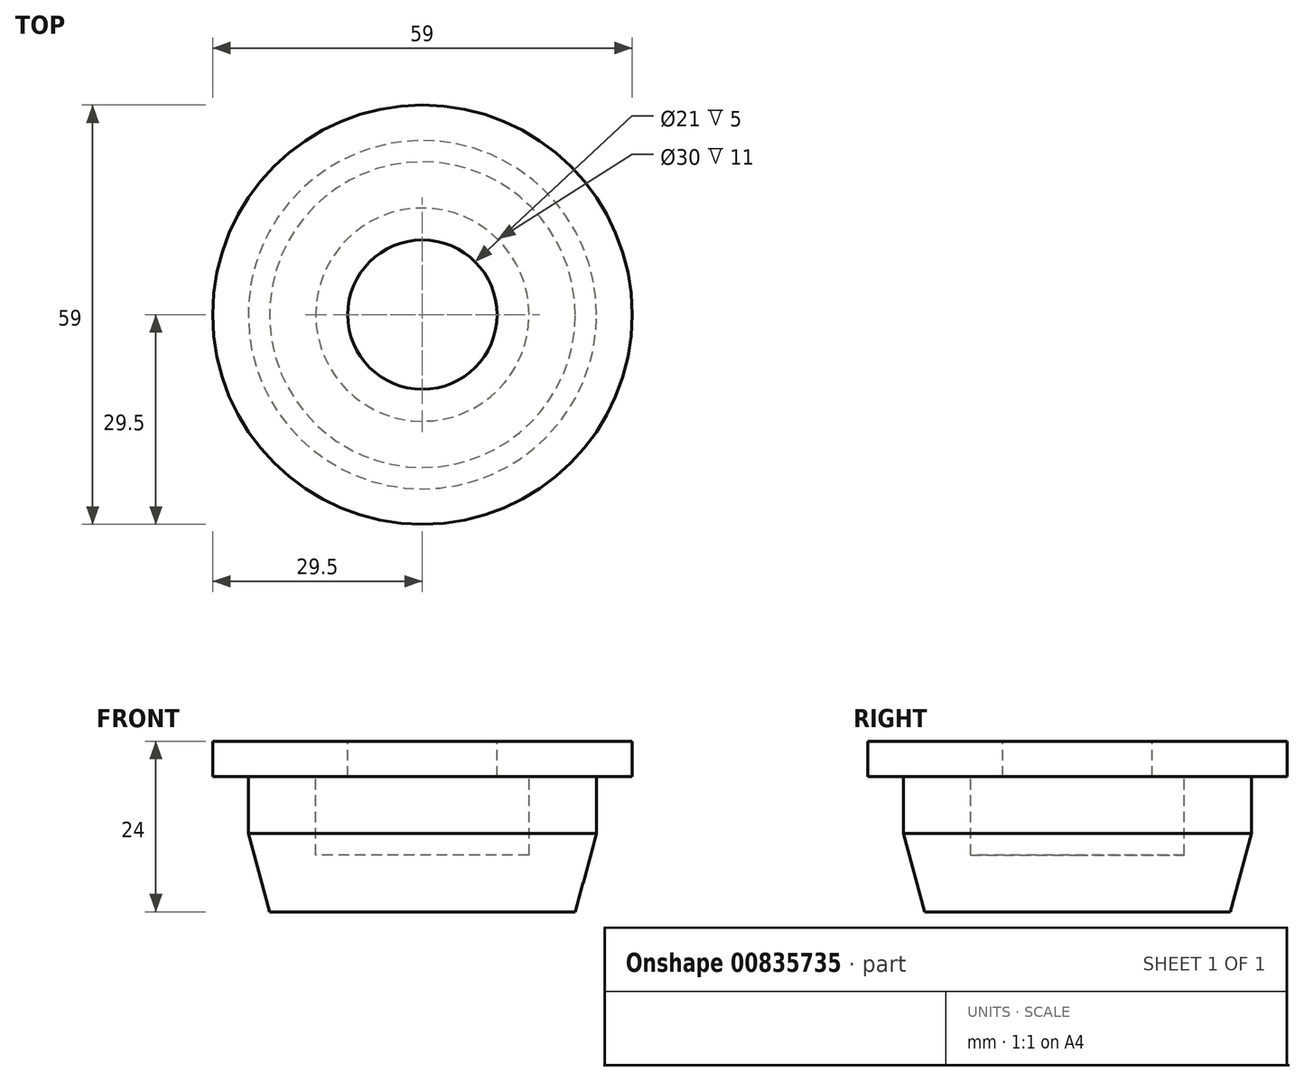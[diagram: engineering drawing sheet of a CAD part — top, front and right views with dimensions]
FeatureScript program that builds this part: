
annotation { "Feature Type Name" : "Feature", "Feature Type Description" : "" }
export const myFeature = defineFeature(function(context is Context, id is Id, definition is map)
    precondition{}
    {
        {
            var Q0;
            Q0=qCreatedBy(makeId("Top.planeOp"),FACE);
            var sketch = newSketch(context, id + "F0", { "sketchPlane" : qUnion([Q0])});
            skCircle(sketch, "E0", {"center": v(0, 0) * mm, "radius": 10.5 * mm});
            skCircle(sketch, "E1", {"center": v(0, 0) * mm, "radius": 24.5 * mm});
            skCircle(sketch, "E2", {"center": v(0, 0) * mm, "radius": 29.5 * mm});
            skCircle(sketch, "E3", {"center": v(0, 0) * mm, "radius": 15 * mm});
            skSolve(sketch);
        }
        {
            var Q0;
            Q0=makeQuery(id+"F0.imprint","IMPRINT",FACE,{"disambiguationData":[TD([[makeQuery(id+"F0.imprint","IMPRINT",EDGE,{"derivedFrom":sQuery(id+"F0.wireOp",EDGE,"E1")}),1.0]])]});
            var Q1;
            Q1=makeQuery(id+"F0.imprint","IMPRINT",FACE,{"disambiguationData":[TD([[makeQuery(id+"F0.imprint","IMPRINT",EDGE,{"derivedFrom":sQuery(id+"F0.wireOp",EDGE,"E0")}),-1.0]])]});
            var Q2;
            Q2=makeQuery(id+"F0.imprint","IMPRINT",FACE,{"disambiguationData":[TD([[makeQuery(id+"F0.imprint","IMPRINT",EDGE,{"derivedFrom":sQuery(id+"F0.wireOp",EDGE,"E0")}),1.0]])]});
            extrude(context, id + "F1", {"entities" : qUnion([Q0, Q1, Q2]), "oppositeDirection" : true, "depth" : 24 * mm, "offsetDistance" : 25 * mm});
        }
        {
            var Q0;
            Q0=makeQuery(id+"F1.opExtrude","CAP_EDGE",EDGE,{"disambiguationData":[OSD([sQuery(id+"F0.wireOp",EDGE,"E1")])],"isStart":false});
            chamfer(context, id + "F2", {"entities" : qUnion([Q0]), "chamferType" : ChamferType.TWO_OFFSETS, "width1" : 11 * mm, "oppositeDirection" : false, "width2" : 3 * mm, "tangentPropagation" : true});
        }
        {
            var Q0;
            Q0 = qSketchRegion(id + "F0", true);
            var Q1;
            Q1=makeQuery(id+"F0.imprint","IMPRINT",FACE,{"disambiguationData":[TD([[makeQuery(id+"F0.imprint","IMPRINT",EDGE,{"derivedFrom":sQuery(id+"F0.wireOp",EDGE,"E0")}),-1.0]])]});
            var Q2;
            Q2=makeQuery(id+"F0.imprint","IMPRINT",FACE,{"disambiguationData":[TD([[makeQuery(id+"F0.imprint","IMPRINT",EDGE,{"derivedFrom":sQuery(id+"F0.wireOp",EDGE,"E0")}),1.0]])]});
            extrude(context, id + "F3", {"entities" : qUnion([Q0, Q1, Q2]), "operationType" : NewBodyOperationType.REMOVE, "oppositeDirection" : true, "depth" : 16 * mm, "offsetDistance" : 25 * mm});
        }
        {
            var Q0;
            Q0=makeQuery(id+"F0.imprint","IMPRINT",FACE,{"disambiguationData":[TD([[makeQuery(id+"F0.imprint","IMPRINT",EDGE,{"derivedFrom":sQuery(id+"F0.wireOp",EDGE,"E0")}),-1.0]])]});
            var Q1;
            Q1=makeQuery(id+"F0.imprint","IMPRINT",FACE,{"disambiguationData":[TD([[makeQuery(id+"F0.imprint","IMPRINT",EDGE,{"derivedFrom":sQuery(id+"F0.wireOp",EDGE,"VLvZryLr-N4DQ-Neu8-7n3T-QVp03Rq5ONKv")}),-1.0]])]});
            extrude(context, id + "F4", {"entities" : qUnion([Q0, Q1]), "operationType" : NewBodyOperationType.ADD, "oppositeDirection" : true, "depth" : 5 * mm, "offsetDistance" : 25 * mm});
        }
        {
            var Q0;
            Q0=makeQuery(id+"F0.imprint","IMPRINT",FACE,{"disambiguationData":[TD([[makeQuery(id+"F0.imprint","IMPRINT",EDGE,{"derivedFrom":sQuery(id+"F0.wireOp",EDGE,"E1")}),-1.0]])]});
            extrude(context, id + "F5", {"entities" : qUnion([Q0]), "operationType" : NewBodyOperationType.ADD, "oppositeDirection" : true, "depth" : 5 * mm, "offsetDistance" : 25 * mm});
        }
    });
